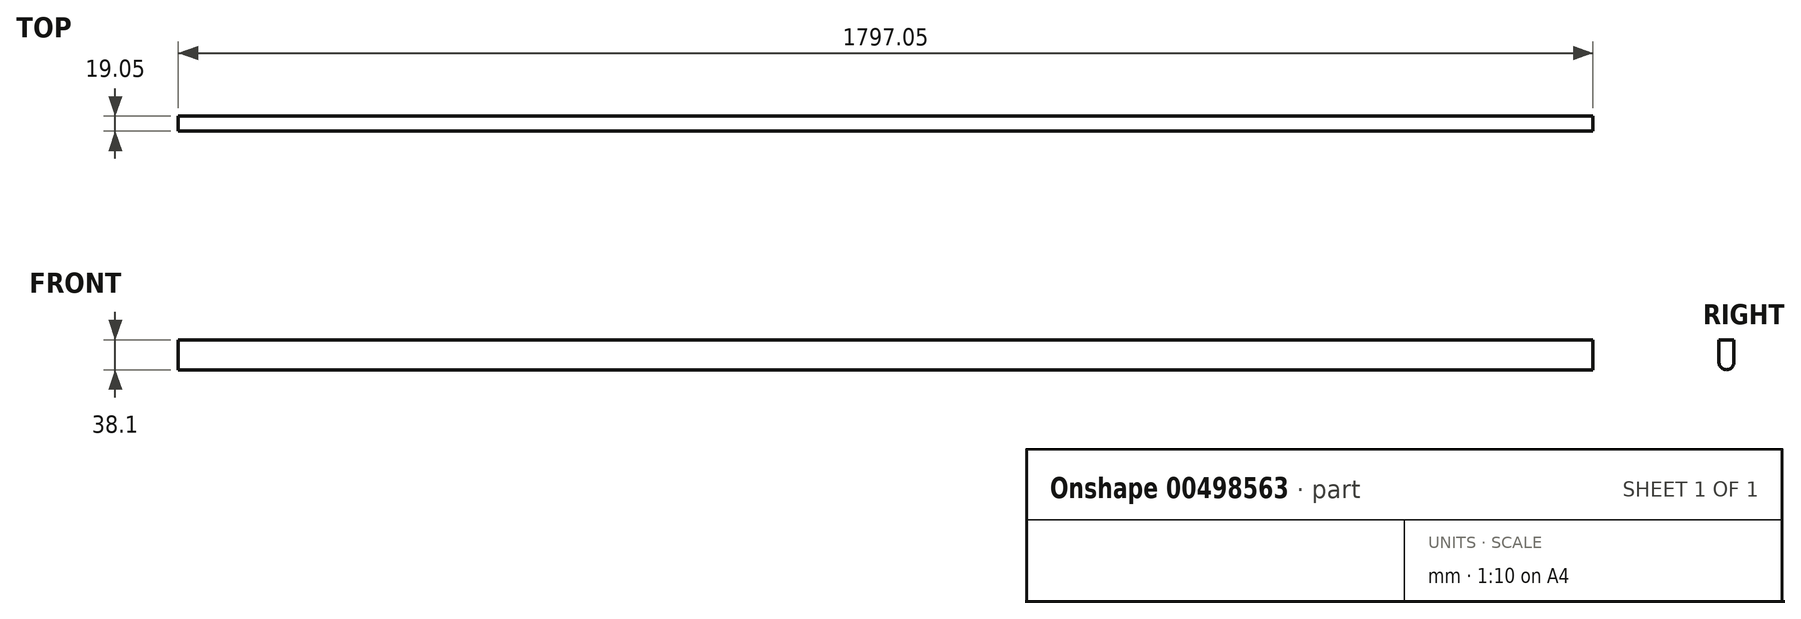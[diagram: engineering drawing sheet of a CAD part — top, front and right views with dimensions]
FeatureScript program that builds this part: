
annotation { "Feature Type Name" : "Feature", "Feature Type Description" : "" }
export const myFeature = defineFeature(function(context is Context, id is Id, definition is map)
    precondition{}
    {
        {
            var Q0;
            Q0=qCreatedBy(makeId("Front.planeOp"),FACE);
            var sketch = newSketch(context, id + "F0", { "sketchPlane" : qUnion([Q0])});
            skLineSegment(sketch, "E0.bottom", {"start": v(0, 0) * mm, "end": v(1797.05, 0) * mm});
            skLineSegment(sketch, "E0.top", {"start": v(0, 38.1) * mm, "end": v(1797.05, 38.1) * mm});
            skLineSegment(sketch, "E0.left", {"start": v(0, 0) * mm, "end": v(0, 38.1) * mm});
            skLineSegment(sketch, "E0.right", {"start": v(1797.05, 0) * mm, "end": v(1797.05, 38.1) * mm});
            skSolve(sketch);
        }
        {
            var Q0;
            Q0 = qSketchRegion(id + "F0", true);
            extrude(context, id + "F1", {"entities" : qUnion([Q0]), "depth" : 19.05 * mm, "offsetDistance" : 25.4 * mm});
        }
        {
            var Q0;
            Q0=makeQuery(id+"F1.opExtrude","CAP_EDGE",EDGE,{"disambiguationData":[OSD([sQuery(id+"F0.wireOp",EDGE,"E0.bottom")])],"isStart":false});
            var Q1;
            Q1=makeQuery(id+"F1.opExtrude","CAP_EDGE",EDGE,{"disambiguationData":[OSD([sQuery(id+"F0.wireOp",EDGE,"E0.bottom")])],"isStart":true});
            fillet(context, id + "F2", {"entities" : qUnion([Q0, Q1]), "radius" : 9.52 * mm, "tangentPropagation" : true, "allowEdgeOverflow" : false});
        }
    });
